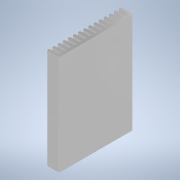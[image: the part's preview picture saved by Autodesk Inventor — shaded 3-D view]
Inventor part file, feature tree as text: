
AUTODESK INVENTOR PART (.ipt)
format: ipt  version: 2020 (Build 240168000, 168)  size: 275,456 bytes
history: native  units: mm
features: fillet x7, other x2, extrude x2, sketch x2, pattern_linear x1
ambient origin geometry x8: Origin, YZ Plane, XZ Plane, XY Plane, X Axis, Y Axis, Z Axis, Center Point
bodies: Body1 (feature_tree)
feature tree (14):
  other  "Bryła1"
  extrude  "Wyciągnięcie proste1"  Depth=10.0mm
  extrude  "Wyciągnięcie proste2"  Depth=5.0mm
  pattern_linear  "Szyk prostokątny1"  Count1=6  [1 undecoded]
  fillet  "Zaokrąglenie1"  Radius=30.0mm
  fillet  "Zaokrąglenie2"  Radius=100.0mm
  fillet  "Zaokrąglenie3"  Radius=2.0mm
  fillet  "Zaokrąglenie4"  Radius=2.0mm
  fillet  "Zaokrąglenie5"  Radius=2.0mm
  fillet  "Zaokrąglenie6"  Radius=100.0mm
  fillet  "Zaokrąglenie7"  Radius=4.15mm
  other  "Pogrubienie1"
  sketch  "Szkic1"
  sketch  "Szkic2"
note: 1 required parameter value undecoded (feature->parameter linkage not recoverable at this tier; creation-order binding heuristic only, values carry confidence <= 0.55)
